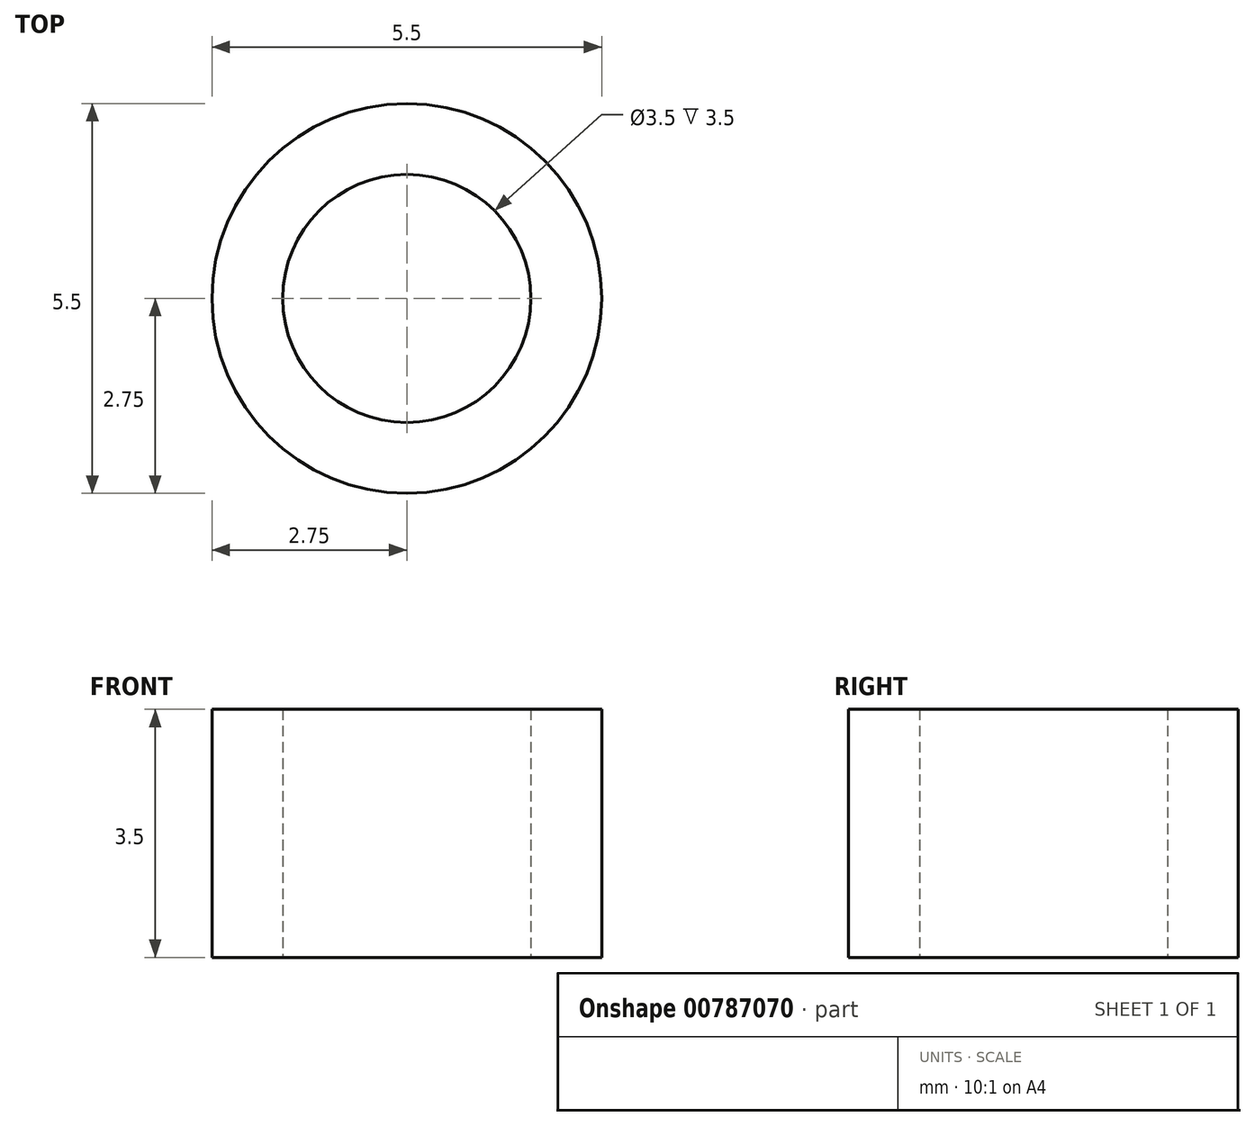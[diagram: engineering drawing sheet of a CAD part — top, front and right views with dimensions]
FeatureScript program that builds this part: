
annotation { "Feature Type Name" : "Feature", "Feature Type Description" : "" }
export const myFeature = defineFeature(function(context is Context, id is Id, definition is map)
    precondition{}
    {
        {
            var Q0;
            Q0=qCreatedBy(makeId("Top.planeOp"),FACE);
            var sketch = newSketch(context, id + "F0", { "sketchPlane" : qUnion([Q0])});
            skCircle(sketch, "E0", {"center": v(0, 0) * mm, "radius": 1.75 * mm});
            skCircle(sketch, "E1", {"center": v(0, 0) * mm, "radius": 2.75 * mm});
            skSolve(sketch);
        }
        {
            var Q0;
            Q0=makeQuery(id+"F0.imprint","IMPRINT",FACE,{"disambiguationData":[TD([[makeQuery(id+"F0.imprint","IMPRINT",EDGE,{"derivedFrom":sQuery(id+"F0.wireOp",EDGE,"E0")}),-1.0]])]});
            extrude(context, id + "F1", {"entities" : qUnion([Q0]), "depth" : 3.5 * mm, "offsetDistance" : 25 * mm});
        }
    });
